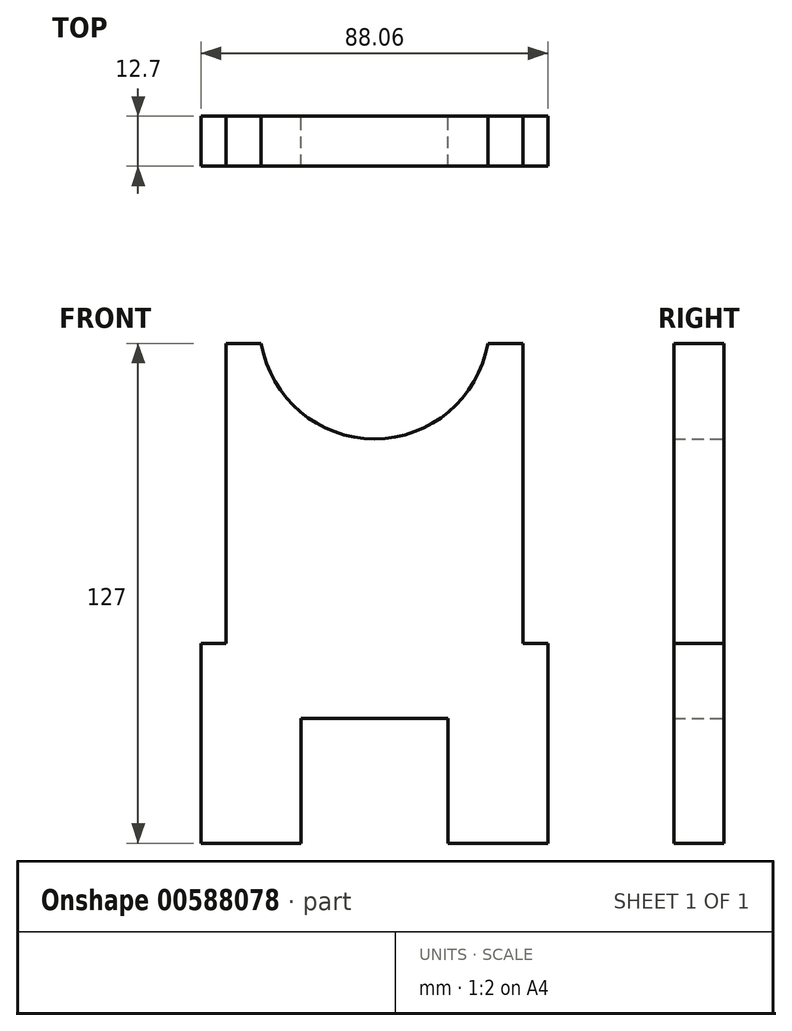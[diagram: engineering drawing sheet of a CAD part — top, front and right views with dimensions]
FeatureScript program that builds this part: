
annotation { "Feature Type Name" : "Feature", "Feature Type Description" : "" }
export const myFeature = defineFeature(function(context is Context, id is Id, definition is map)
    precondition{}
    {
        {
            var Q0;
            Q0=qCreatedBy(makeId("Front.planeOp"),FACE);
            var sketch = newSketch(context, id + "F0", { "sketchPlane" : qUnion([Q0])});
            skLineSegment(sketch, "E0", {"start": v(-44.45, 25.4) * mm, "end": v(-44.45, 76.2) * mm});
            skLineSegment(sketch, "E1", {"start": v(-44.45, 76.2) * mm, "end": v(-38.1, 76.2) * mm});
            skLineSegment(sketch, "E2", {"start": v(-38.1, 76.2) * mm, "end": v(-38.1, 152.4) * mm});
            skLineSegment(sketch, "E3", {"start": v(43.6, 25.4) * mm, "end": v(43.6, 76.2) * mm});
            skLineSegment(sketch, "E4", {"start": v(43.6, 76.2) * mm, "end": v(37.26, 76.2) * mm});
            skLineSegment(sketch, "E5", {"start": v(37.26, 76.2) * mm, "end": v(37.26, 152.4) * mm});
            skLineSegment(sketch, "E6", {"start": v(-19.05, 25.4) * mm, "end": v(-19.05, 57.15) * mm});
            skLineSegment(sketch, "E7", {"start": v(-19.05, 57.15) * mm, "end": v(18.2, 57.15) * mm});
            skLineSegment(sketch, "E8", {"start": v(18.2, 57.15) * mm, "end": v(18.2, 25.4) * mm});
            skLineSegment(sketch, "E9", {"start": v(-19.05, 25.4) * mm, "end": v(-44.45, 25.4) * mm});
            skLineSegment(sketch, "E10", {"start": v(18.2, 25.4) * mm, "end": v(43.6, 25.4) * mm});
            skLineSegment(sketch, "E11", {"start": v(-38.1, 152.4) * mm, "end": v(-29.21, 152.4) * mm});
            skLineSegment(sketch, "E12", {"start": v(37.26, 152.4) * mm, "end": v(28.37, 152.4) * mm});
            skArc(sketch, "E13", {"start": v(-29.21, 152.4) * mm, "mid": v(-0.42, 128.13) * mm, "end": v(28.37, 152.4) * mm});
            skSolve(sketch);
        }
        {
            var Q0;
            Q0=makeQuery(id+"F0.imprint","IMPRINT",FACE,{"disambiguationData":[TD([[makeQuery(id+"F0.imprint","IMPRINT",EDGE,{"derivedFrom":sQuery(id+"F0.wireOp",EDGE,"E0")}),-1.0]])]});
            extrude(context, id + "F1", {"entities" : qUnion([Q0]), "depth" : 12.7 * mm, "offsetDistance" : 25.4 * mm});
        }
    });
